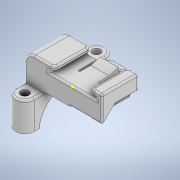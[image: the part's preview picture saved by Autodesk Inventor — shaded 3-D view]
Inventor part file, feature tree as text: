
AUTODESK INVENTOR PART (.ipt)
format: ipt  version: 2020.3 (Build 243373000, 373)  size: 477,696 bytes
history: native  units: mm
features: fillet x13, sketch x9, extrude x8
ambient origin geometry x8: Origin, YZ Plane, XZ Plane, XY Plane, X Axis, Y Axis, Z Axis, Center Point
bodies: Volumenkörper1 (feature_tree)
feature tree (30):
  extrude  "Extrusion1"  Depth=24.0mm
  extrude  "Extrusion2"  Depth=2.0mm
  extrude  "Extrusion3"  Depth=10.0mm
  fillet  "Rundung1"  Radius=20.0mm
  fillet  "Rundung2"  Radius=49.0mm
  fillet  "Rundung3"  Radius=15.8mm
  fillet  "Rundung4"  Radius=32.0mm
  fillet  "Rundung5"  Radius=18.0mm
  fillet  "Rundung6"  Radius=10.0mm
  extrude  "Extrusion4"  Depth=15.8mm
  extrude  "Extrusion5"  Depth=10.0mm
  sketch  "Skizze6"  dims[d19=4.5mm d20=5.0mm]
  extrude  "Extrusion6"  Depth=5.0mm
  extrude  "Extrusion7"  Depth=5.0mm
  fillet  "Rundung7"  Radius=5.0mm
  extrude  "Extrusion8"  Depth=27.0mm
  fillet  "Rundung8"  Radius=5.0mm
  fillet  "Rundung10"  Radius=3.0mm
  fillet  "Rundung11"  Radius=5.0mm
  fillet  "Rundung12"  Radius=1.0mm
  fillet  "Rundung13"  Radius=2.0mm
  fillet  "Rundung14"  Radius=1.0mm
  sketch  "Skizze1"  dims[d0=20.0mm d2=24.0mm]
  sketch  "Skizze2"  dims[d3=32.0mm d4=2.0mm]
  sketch  "Skizze3"  dims[d5=2.0mm d6=2.0mm d7=20.0mm d8=0.0mm d9=49.0mm d10=15.8mm d11=32.0mm d12=18.0mm d13=10.0mm]
  sketch  "Skizze4"  dims[d14=24.5mm d15=15.8mm]
  sketch  "Skizze5"  dims[d16=10.0mm d17=0.0mm d18=4.5mm]
  sketch  "Skizze7"  dims[d21=5.0mm d22=5.0mm d23=5.0mm]
  sketch  "Skizze8"  dims[d24=0.0mm d25=0.0mm d26=27.0mm d27=5.0mm d28=3.0mm d29=5.0mm d30=1.0mm d31=2.0mm d32=1.0mm]
  sketch  "Skizze9"  dims[d33=10.0mm d34=1.0mm d35=1.0mm d36=13.129033mm d37=11.0mm d38=5.0mm d39=10.0mm d40=0.0mm d41=1.5mm d42=5.0mm d43=2.0mm d44=4.363323mm d45=7.0mm d46=10.0mm d47=0.0mm d48=1.5mm d49=0.0mm d51=10.2mm d52=7.0mm d53=10.0mm d54=0.0mm d55=5.0mm d57=10.0mm d58=7.0mm d59=5.0mm d60=3.0mm d61=10.0mm d62=0.0mm d63=1.0mm d65=1.0mm d66=1.0mm d67=2.0mm d68=0.5mm d69=10.0mm d70=26.0mm d71=0.5mm d72=3.0mm]
